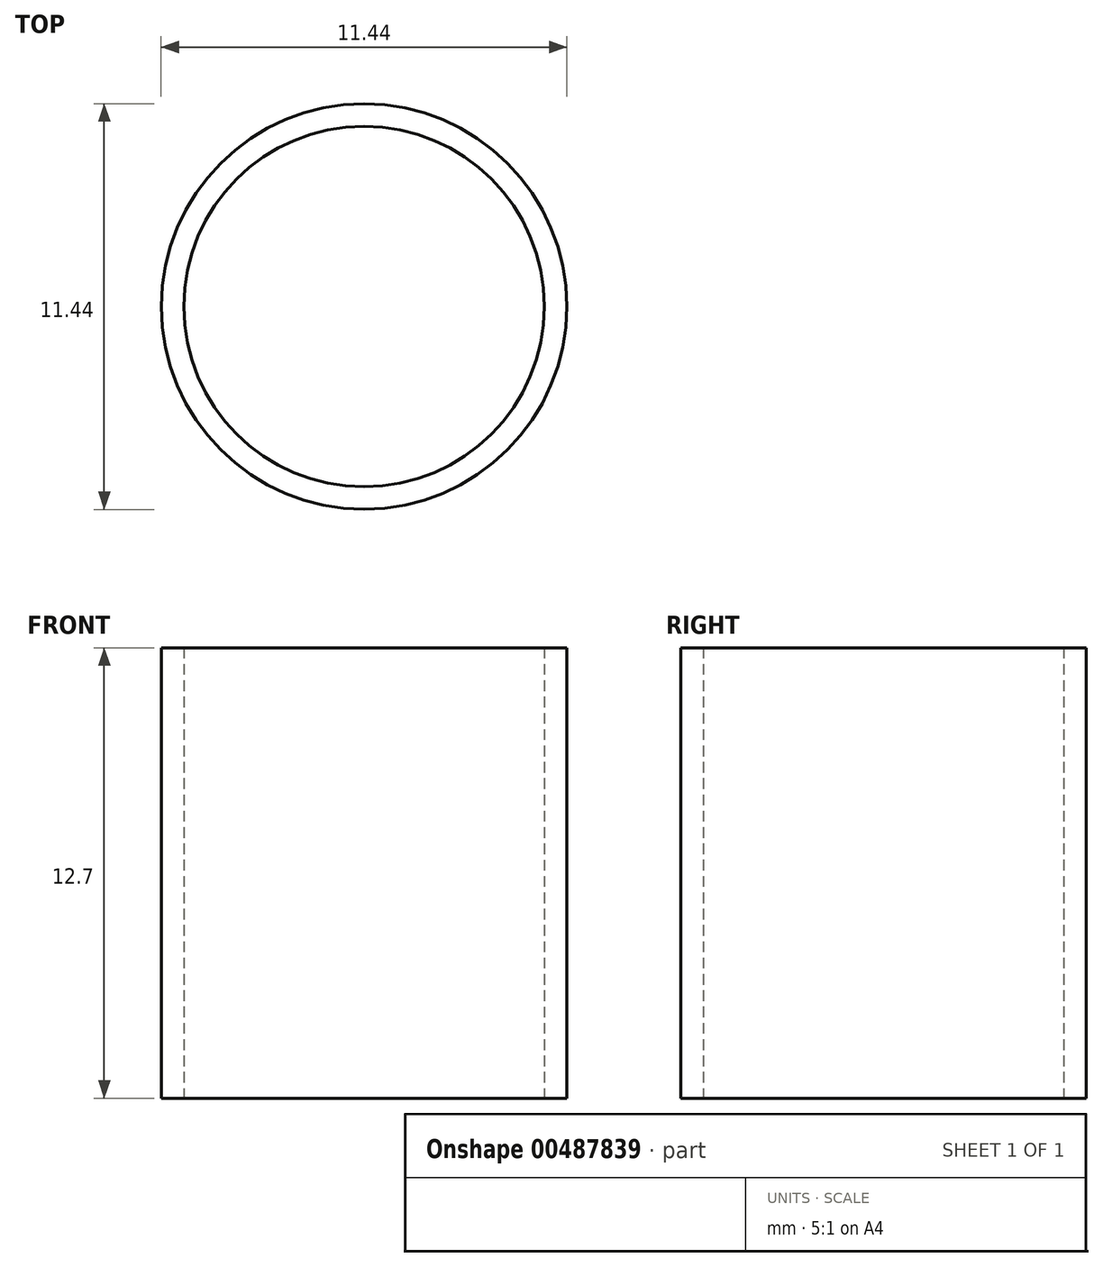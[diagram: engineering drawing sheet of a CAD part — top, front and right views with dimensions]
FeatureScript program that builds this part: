
annotation { "Feature Type Name" : "Feature", "Feature Type Description" : "" }
export const myFeature = defineFeature(function(context is Context, id is Id, definition is map)
    precondition{}
    {
        {
            var Q0;
            Q0=qCreatedBy(makeId("Top.planeOp"),FACE);
            var sketch = newSketch(context, id + "F0", { "sketchPlane" : qUnion([Q0])});
            skCircle(sketch, "E0", {"center": v(0, 0) * mm, "radius": 5.08 * mm});
            skCircle(sketch, "E1", {"center": v(0, 0) * mm, "radius": 5.72 * mm});
            skSolve(sketch);
        }
        {
            var Q0;
            Q0 = qSketchRegion(id + "F0", true);
            extrude(context, id + "F1", {"entities" : qUnion([Q0]), "depth" : 12.7 * mm});
        }
    });
